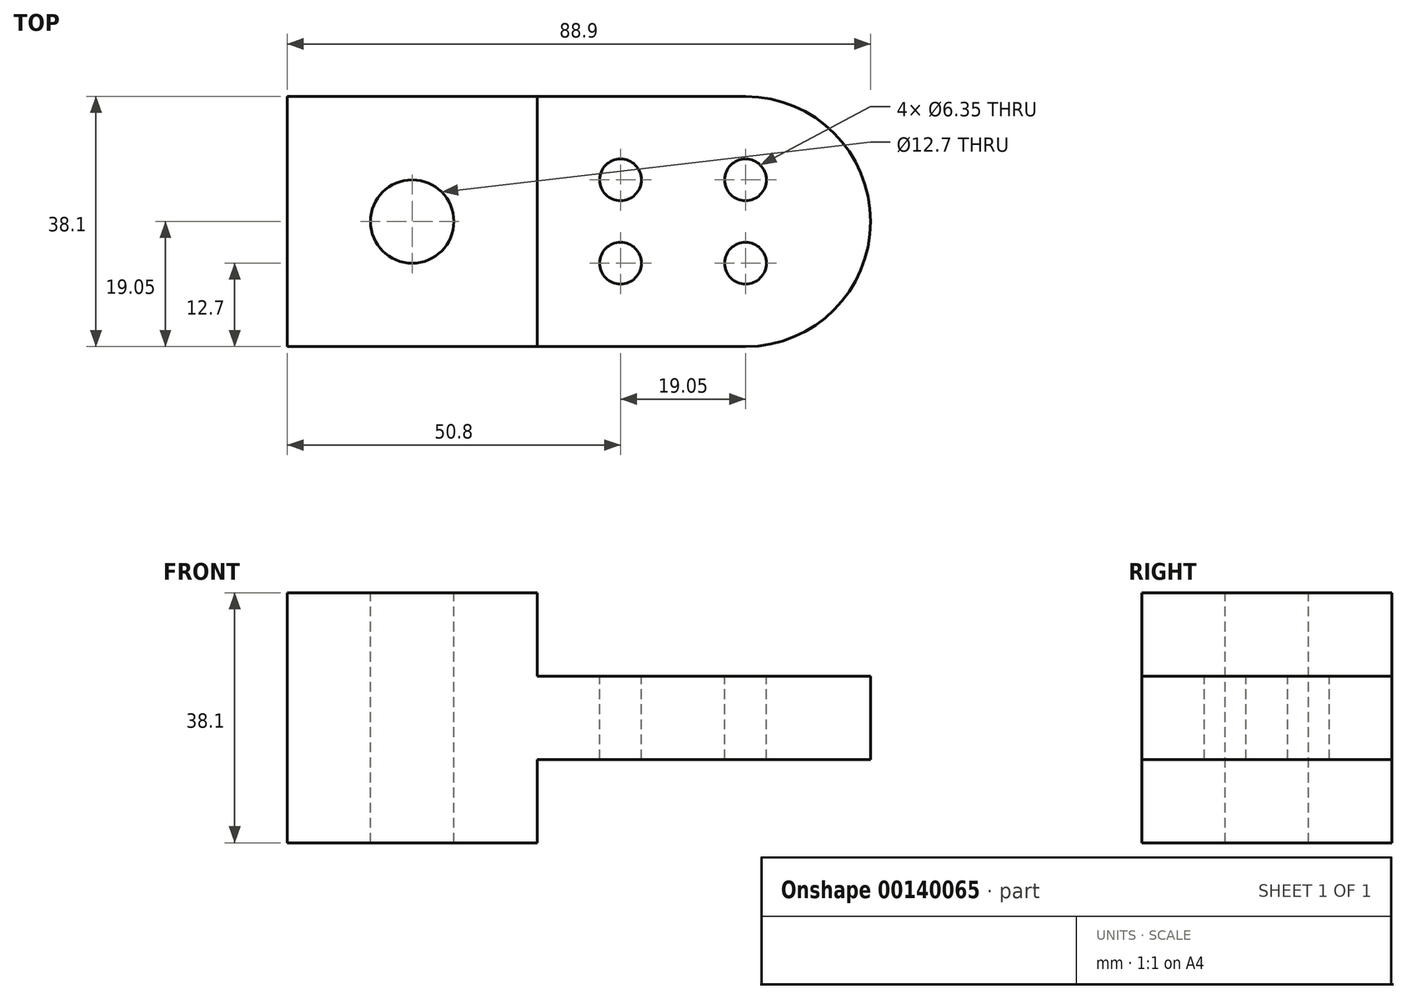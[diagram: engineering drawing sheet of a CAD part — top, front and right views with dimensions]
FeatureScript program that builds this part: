
annotation { "Feature Type Name" : "Feature", "Feature Type Description" : "" }
export const myFeature = defineFeature(function(context is Context, id is Id, definition is map)
    precondition{}
    {
        {
            var Q0;
            Q0=qCreatedBy(makeId("Front.planeOp"),FACE);
            var sketch = newSketch(context, id + "F0", { "sketchPlane" : qUnion([Q0])});
            skLineSegment(sketch, "E0", {"start": v(0, 0) * mm, "end": v(38.1, 0) * mm});
            skLineSegment(sketch, "E1", {"start": v(38.1, 0) * mm, "end": v(38.1, 12.7) * mm});
            skLineSegment(sketch, "E2", {"start": v(38.1, 12.7) * mm, "end": v(88.9, 12.7) * mm});
            skLineSegment(sketch, "E3", {"start": v(88.9, 12.7) * mm, "end": v(88.9, 25.4) * mm});
            skLineSegment(sketch, "E4", {"start": v(88.9, 25.4) * mm, "end": v(38.1, 25.4) * mm});
            skLineSegment(sketch, "E5", {"start": v(38.1, 25.4) * mm, "end": v(38.1, 38.1) * mm});
            skLineSegment(sketch, "E6", {"start": v(38.1, 38.1) * mm, "end": v(0, 38.1) * mm});
            skLineSegment(sketch, "E7", {"start": v(0, 38.1) * mm, "end": v(0, 0) * mm});
            skSolve(sketch);
        }
        {
            var Q0;
            Q0 = qSketchRegion(id + "F0", true);
            extrude(context, id + "F1", {"entities" : qUnion([Q0]), "depth" : 38.1 * mm});
        }
        {
            var Q0;
            Q0=makeQuery(id+"F1.opExtrude","SWEPT_FACE",FACE,{"disambiguationData":[OSD([sQuery(id+"F0.wireOp",EDGE,"E6")])]});
            var sketch = newSketch(context, id + "F2", { "sketchPlane" : qUnion([Q0])});
            skCircle(sketch, "E8", {"center": v(19.05, -19.05) * mm, "radius": 6.35 * mm});
            skPoint(sketch, "E8.centerSnap0", {"position": v(38.1, -19.05) * mm});
            skPoint(sketch, "E8.centerSnap1", {"position": v(19.05, 0) * mm});
            skLineSegment(sketch, "E9", {"start": v(0, -19.05) * mm, "end": v(93.78, -19.05) * mm, "construction": true});
            skLineSegment(sketch, "E10", {"start": v(38.1, -12.7) * mm, "end": v(90.97, -12.7) * mm, "construction": true});
            skLineSegment(sketch, "E11", {"start": v(38.1, -25.4) * mm, "end": v(92.3, -25.4) * mm, "construction": true});
            skLineSegment(sketch, "E12.0.0", {"start": v(69.85, 0) * mm, "end": v(38.1, 0) * mm});
            skLineSegment(sketch, "E12.0.1", {"start": v(38.1, 0) * mm, "end": v(38.1, -38.1) * mm});
            skLineSegment(sketch, "E12.0.2", {"start": v(38.1, -38.1) * mm, "end": v(88.9, -38.1) * mm});
            skLineSegment(sketch, "E12.0.3", {"start": v(88.9, -38.1) * mm, "end": v(88.9, -19.05) * mm});
            skCircle(sketch, "E13", {"center": v(50.8, -12.7) * mm, "radius": 3.18 * mm});
            skCircle(sketch, "E14", {"center": v(69.85, -12.7) * mm, "radius": 3.18 * mm});
            skCircle(sketch, "E15", {"center": v(50.8, -25.4) * mm, "radius": 3.18 * mm});
            skCircle(sketch, "E16", {"center": v(69.85, -25.4) * mm, "radius": 3.18 * mm});
            skPoint(sketch, "E17.visualSharp", {"position": v(88.9, 0) * mm});
            skArc(sketch, "E17.filletArc", {"start": v(88.9, -19.05) * mm, "mid": v(83.32, -5.58) * mm, "end": v(69.85, 0) * mm});
            skSolve(sketch);
        }
        {
            var Q0;
            Q0=makeQuery(id+"F2.imprint","IMPRINT",FACE,{"disambiguationData":[TD([[makeQuery(id+"F2.imprint","IMPRINT",EDGE,{"derivedFrom":sQuery(id+"F2.wireOp",EDGE,"E8")}),1.0]])]});
            var Q1;
            Q1=makeQuery(id+"F2.imprint","IMPRINT",FACE,{"disambiguationData":[TD([[makeQuery(id+"F2.imprint","IMPRINT",EDGE,{"derivedFrom":sQuery(id+"F2.wireOp",EDGE,"E13")}),1.0]])]});
            var Q2;
            Q2=makeQuery(id+"F2.imprint","IMPRINT",FACE,{"disambiguationData":[TD([[makeQuery(id+"F2.imprint","IMPRINT",EDGE,{"derivedFrom":sQuery(id+"F2.wireOp",EDGE,"E15")}),1.0]])]});
            var Q3;
            Q3=makeQuery(id+"F2.imprint","IMPRINT",FACE,{"disambiguationData":[TD([[makeQuery(id+"F2.imprint","IMPRINT",EDGE,{"derivedFrom":sQuery(id+"F2.wireOp",EDGE,"E16")}),1.0]])]});
            var Q4;
            Q4=makeQuery(id+"F2.imprint","IMPRINT",FACE,{"disambiguationData":[TD([[makeQuery(id+"F2.imprint","IMPRINT",EDGE,{"derivedFrom":sQuery(id+"F2.wireOp",EDGE,"E14")}),1.0]])]});
            extrude(context, id + "F3", {"entities" : qUnion([Q0, Q1, Q2, Q3, Q4]), "operationType" : NewBodyOperationType.REMOVE, "endBound" : BoundingType.THROUGH_ALL, "oppositeDirection" : true, "depth" : 25.4 * mm});
        }
        {
            var Q0;
            Q0=makeQuery(id+"F1.opExtrude","CAP_EDGE",EDGE,{"disambiguationData":[OSD([sQuery(id+"F0.wireOp",EDGE,"E3")])],"isStart":true});
            var Q1;
            Q1=makeQuery(id+"F1.opExtrude","CAP_EDGE",EDGE,{"disambiguationData":[OSD([sQuery(id+"F0.wireOp",EDGE,"E3")])],"isStart":false});
            fillet(context, id + "F4", {"entities" : qUnion([Q0, Q1]), "radius" : 19.05 * mm, "tangentPropagation" : true, "allowEdgeOverflow" : false});
        }
    });
